# Revit family: 3f_filippi_-_3f_lem_ho_ampio_3f_filippi_-_58955_a0812_-_3f_lem_3_ho_led_210_cr_ampio___vs_6a1d
name_source: partatom
category: Lighting Fixtures
units: mm (PartAtom-declared; Revit-internal decimal feet)

## family parameters
Cut with Voids When Loaded = No
Host = Face
Light Source = No
Part Type = Normal
Room Calculation Point = No
Round Connector Dimension = Use Diameter
Shared = No

## types (1)
- 3F Filippi - 3F LEM HO Ampio (1 x LED, 26553 lm, 207 W, 4000 K)
    Apparent Load = 207 VA
    Approval mark = CE
    CIE Flux Codes = 67 90 97 100 100
    Color Rendering = 80
    Color Temperature = 4000 K
    Control Gear = Electronic ballast
    Default Elevation = 1800 mm
    Description = Industrial luminaire with high light output and high luminous efficiency designed with the most innovative technologies for environments with temperature up to 55°C.

ILLUMINOTECHNICAL
Luminous efficiency 100% (DLOR 98%, ULOR 2%).
Initial luminous flux of the luminaire 26553 lm.
Direct symmetric wide distribution: the illuminated area has a rectangular shape.
Installation Interdistance Transv.D = 1.24 x hu - Long.D = 1.20 x hu.
Tabular UGR (CIE 117 - 4H-8H; S=0.25H; 70/50/20): RUG 23.8 - 23.9.
Beam angle: 82° - 83°.
Luminous efficacy 128 lm/W.
Lifetime (L93/B10): 30000 h. (tq+25°C)
Lifetime (L90/B10): 50000 h. (tq+25°C)
Lifetime (L85/B10): 80000 h. (tq+25°C)
Lifetime (L80/B10): 100000 h. (tq+25°C)
Lifetime (L85/B10): 50000 h. (tq+55°C)
Sudden decreased luminous flux after 50000 hours: 0% (C0).
Photobiological safety in compliance with IEC/TR 62778: RG0 risk exempt, (IEC 62471).
In compliance with IEC/EN 62722-2-1 - IEC/EN 62717 standards.

SOURCE
3 Mid-Power linear LED modules 70W/840.
Energy efficiency class (UE 2019/2020 - UE 2019/2015): C.
CIE 13.3 Colour rendering index: CRI >80 (R9 <50%).
IES TM-30 Fidelity Index: Rf = 84 Rg = 95.
CCT nominal colour temperature 4000 K.
Colour initial tolerance (MacAdam): SDCM 3.

MECHANICAL
Passive modular heatsinks in die-casted aluminium, painted in white colour.
To optimize the thermal management of the LED module, the heatsinks are oversized and provided with self-cleaning of cooling fins.
Wiring body in aluminium and galvanised steel anchored solidly to the sinks and thermally separated.
3F Lens lenses with high luminous efficiency, transparent methacrylate (PMMA), fixed to the LED modules.
Fixing brackets in stainless steel.
Luminaire with limited surface temperature. - D - (EN 60598-2-24)
Dimensions: 657x542 mm, height 133 mm. Weight 15.125 kg.
IP65 protection degree.
Mechanical strength to impacts IK06 (1 joule).
Glow-wire test resistance 650°C.

ELECTRICAL
Halogen Free electronic wiring 230V-50/60Hz, power factor 0.97, THD <25%, constant output current, class I, 2 driver.
Power of the luminaire 207 W.
ENEC - CE.
SAFE FLICKER: PstLM=<1 and SVM=<0.4 (IEC TR 61547-1 and IEC TR 63158), to ensure a more comfortable and safe light.
Luminaire compliant with EN 60598-2-22 for power supply from a centralised emergency system CPSS (Central Power Supply System), not incorporated in the luminaire - high risk areas excluded. The default power and flux are 100% in AC and 100% in DC.
Ambient temperature from -30°C to +55°C.
Temperature class T6 max 85°C.
Quick connection via M20 3P connector with 9-13 mm tightening range.
Power unit positioned on a separate compartment by the LED module to ensure optimum temperatures of cabling components, to be inspectable and maintainable.
Relative humidity UR: <85%.

INSTALLATION
Ceiling / Suspended / Wall.
All accessories dedicated to this product are available on the Catalog and on our website www.3F-Filippi.com.

ACCESSORIES
A0812 - Anti-glare microprismatic VS moulded glass, tempered, not flammable, with sealing gasket.
One required for each light module. The pack contains 10 pieces.

APPLICATIONS
In commercial environments, exhibition and industrial areas, stores, open areas.
Environments in which it is necessary a total protection against falling fragments (eg environments with foodstuffs or machines with moving parts or with extreme temperature changes), use luminaires with polycarbonate lenses.

WARNING
Fixture not suitable for cold stores with an ambient temperature <0°C and/or relative humidity >85%.
Luminaire designed for disposal/recycling at end-of-life.
Replaceable (LED only) light source by a professional. Replaceable control gear by a professional.
    Height = 133 mm  [stored 0.436352 ft]
    Lamp = 1 x LED
    Lamp Light Flux = 26553 lm
    Lamp Power = 207 W
    Lamp count = 1
    Length = 657 mm
    Lifetime = 50000 h
    Luminous efficacy = 128 lm/W
    Manufacturer = 3F Filippi
    ModVariant = No
    Model = 3F Filippi - 58955+A0812 - 3F LEM 3 HO LED 210 CR AMPIO + VS
    Mounting Place = Ceiling
    Mounting Type = Pendant
    Number of Poles = 1
    OnlyDefault = Yes
    Power Factor = 1
    Product Name = 3F Filippi - 3F LEM HO Ampio
    Product group = pendant luminaire
    ProductGroupID = 9
    Protection Class = Protection class I
    Protection Degree = IP 65
    RLX_Detail_Level = 1
    RLX_Emergency_Light_Flux = 0 lm
    RLX_Emergency_Type = 0
    RLX_Emergency_Type_DB = No
    RlxData = <blob elided: 110045 chars, md5=e1e1ef70>
    Socket = socket
    Standby Power = 0 W
    System Light Flux = 26553 lm
    System Power = 207 W
    Type Comments = Product without accessories
    Type Image = 3f_filippi_-_lem_3__a0812.jpg
    URL = http://relux.com
    VarID = ---
    Voltage = 0 V
    Weight = 0.00 kg
    Width = 542 mm

note: [stored X ft] marks values corroborated as IEEE doubles in the binary element streams (Revit-internal decimal feet)

## geometry (parser evidence)
native form markers: Sweep x11
no freeform markers — native parametric forms only
